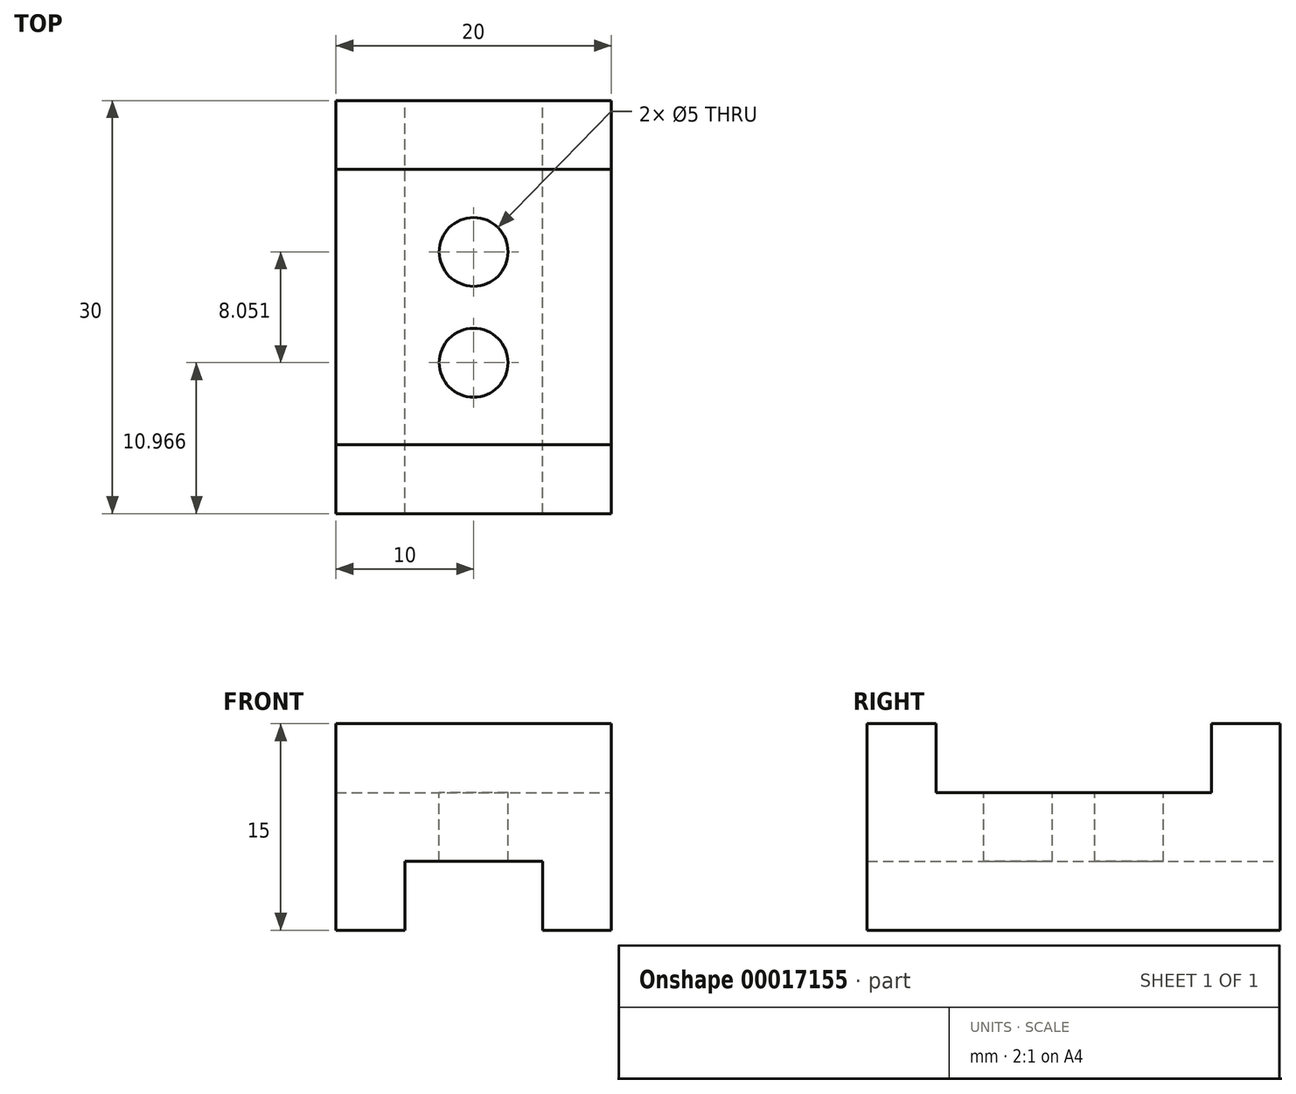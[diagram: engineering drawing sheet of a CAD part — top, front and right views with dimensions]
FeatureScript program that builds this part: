
annotation { "Feature Type Name" : "Feature", "Feature Type Description" : "" }
export const myFeature = defineFeature(function(context is Context, id is Id, definition is map)
    precondition{}
    {
        {
            var Q0;
            Q0=qCreatedBy(makeId("Front.planeOp"),FACE);
            var sketch = newSketch(context, id + "F0", { "sketchPlane" : qUnion([Q0])});
            skLineSegment(sketch, "E0", {"start": v(-20, -12.38) * mm, "end": v(-15, -12.38) * mm});
            skLineSegment(sketch, "E1", {"start": v(-15, -12.38) * mm, "end": v(-15, -7.38) * mm});
            skLineSegment(sketch, "E2", {"start": v(-15, -7.38) * mm, "end": v(-5, -7.38) * mm});
            skLineSegment(sketch, "E3", {"start": v(-5, -7.38) * mm, "end": v(-5, -12.38) * mm});
            skLineSegment(sketch, "E4", {"start": v(-5, -12.38) * mm, "end": v(0, -12.38) * mm});
            skLineSegment(sketch, "E5", {"start": v(0, -12.38) * mm, "end": v(0, -2.38) * mm});
            skLineSegment(sketch, "E6", {"start": v(0, -2.38) * mm, "end": v(-20, -2.38) * mm});
            skLineSegment(sketch, "E7", {"start": v(-20, -2.38) * mm, "end": v(-20, -12.38) * mm});
            skSolve(sketch);
        }
        {
            var Q0;
            Q0 = qSketchRegion(id + "F0", true);
            extrude(context, id + "F1", {"entities" : qUnion([Q0]), "depth" : 30 * mm});
        }
        {
            var Q0;
            Q0=makeQuery(id+"F1.opExtrude","SWEPT_FACE",FACE,{"disambiguationData":[OSD([sQuery(id+"F0.wireOp",EDGE,"E6")])]});
            var sketch = newSketch(context, id + "F2", { "sketchPlane" : qUnion([Q0])});
            skLineSegment(sketch, "E8.bottom", {"start": v(-20, 0) * mm, "end": v(0, 0) * mm});
            skLineSegment(sketch, "E8.top", {"start": v(-20, -5) * mm, "end": v(0, -5) * mm});
            skLineSegment(sketch, "E8.left", {"start": v(-20, 0) * mm, "end": v(-20, -5) * mm});
            skLineSegment(sketch, "E8.right", {"start": v(0, 0) * mm, "end": v(0, -5) * mm});
            skLineSegment(sketch, "E9.bottom", {"start": v(-20, -30) * mm, "end": v(0, -30) * mm});
            skLineSegment(sketch, "E9.top", {"start": v(-20, -25) * mm, "end": v(0, -25) * mm});
            skLineSegment(sketch, "E9.left", {"start": v(-20, -30) * mm, "end": v(-20, -25) * mm});
            skLineSegment(sketch, "E9.right", {"start": v(0, -30) * mm, "end": v(0, -25) * mm});
            skSolve(sketch);
        }
        {
            var Q0;
            Q0 = qSketchRegion(id + "F2", true);
            extrude(context, id + "F3", {"entities" : qUnion([Q0]), "operationType" : NewBodyOperationType.ADD, "depth" : 5 * mm});
        }
        {
            var Q0;
            Q0=makeQuery(id+"F1.opExtrude","SWEPT_FACE",FACE,{"disambiguationData":[OSD([sQuery(id+"F0.wireOp",EDGE,"E6")])]});
            var sketch = newSketch(context, id + "F4", { "sketchPlane" : qUnion([Q0])});
            skCircle(sketch, "E10", {"center": v(-10, -10.98) * mm, "radius": 2.5 * mm});
            skCircle(sketch, "E11", {"center": v(-10, -19.03) * mm, "radius": 2.5 * mm});
            skSolve(sketch);
        }
        {
            var Q0;
            Q0=makeQuery(id+"F4.imprint","IMPRINT",FACE,{"disambiguationData":[TD([[makeQuery(id+"F4.imprint","IMPRINT",EDGE,{"derivedFrom":sQuery(id+"F4.wireOp",EDGE,"E11")}),1.0]])]});
            var Q1;
            Q1=makeQuery(id+"F4.imprint","IMPRINT",FACE,{"disambiguationData":[TD([[makeQuery(id+"F4.imprint","IMPRINT",EDGE,{"derivedFrom":sQuery(id+"F4.wireOp",EDGE,"E10")}),1.0]])]});
            extrude(context, id + "F5", {"entities" : qUnion([Q0, Q1]), "operationType" : NewBodyOperationType.REMOVE, "endBound" : BoundingType.THROUGH_ALL, "oppositeDirection" : true, "depth" : 25 * mm});
        }
    });
